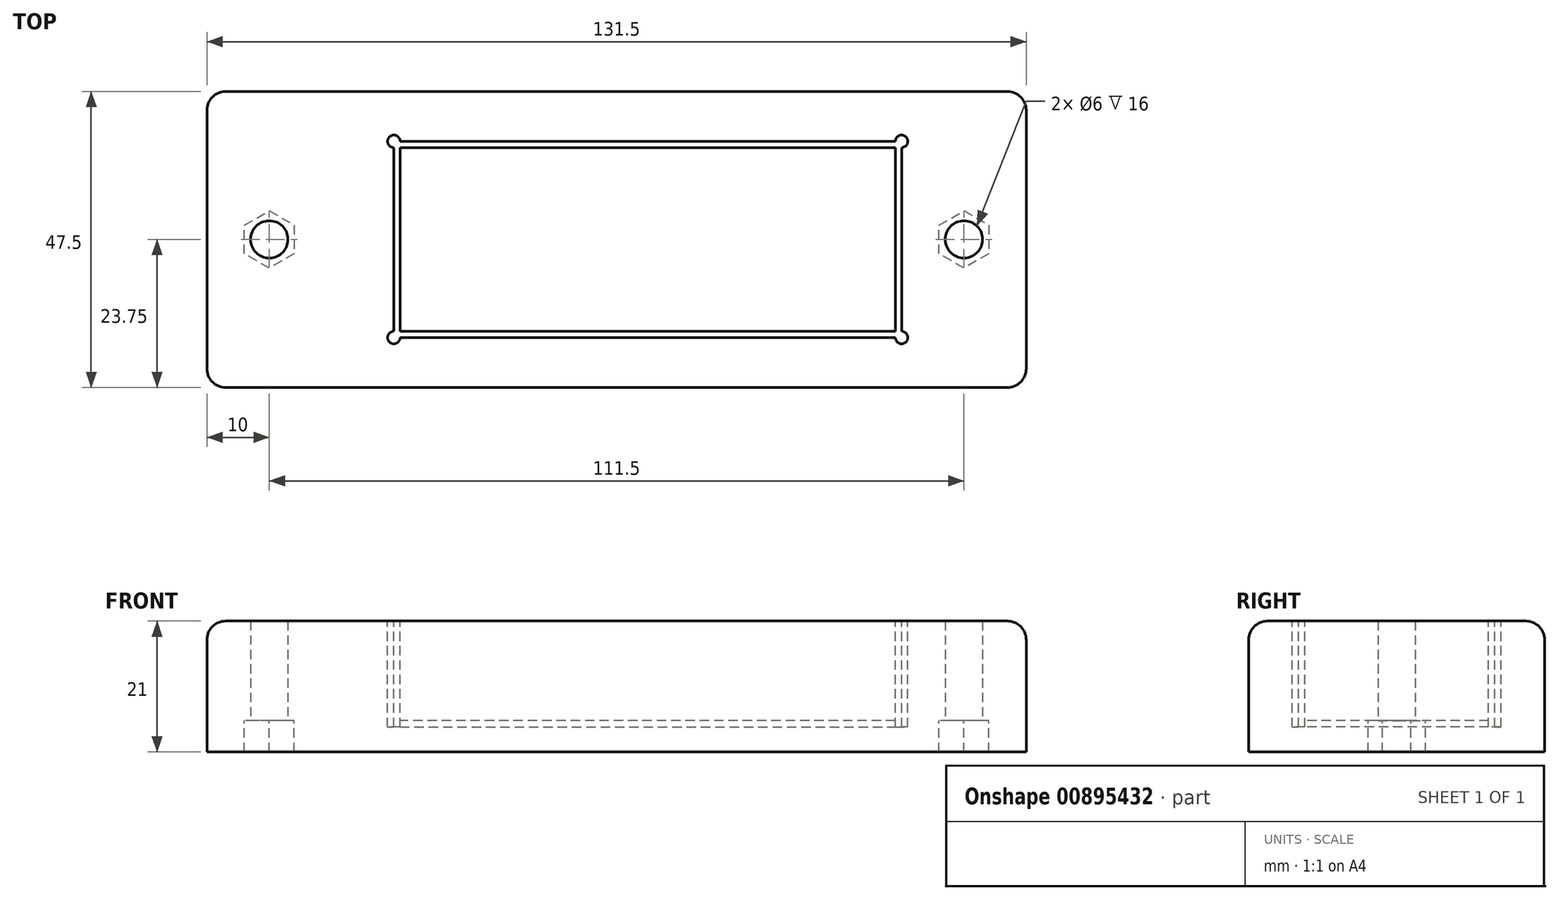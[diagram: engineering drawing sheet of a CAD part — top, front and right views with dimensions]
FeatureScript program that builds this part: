
annotation { "Feature Type Name" : "Feature", "Feature Type Description" : "" }
export const myFeature = defineFeature(function(context is Context, id is Id, definition is map)
    precondition{}
    {
        {
            var Q0;
            Q0=qCreatedBy(makeId("Top.planeOp"),FACE);
            var sketch = newSketch(context, id + "F0", { "sketchPlane" : qUnion([Q0])});
            skLineSegment(sketch, "E0.bottom", {"start": v(-35.75, 15.75) * mm, "end": v(40.25, 15.75) * mm});
            skLineSegment(sketch, "E0.top", {"start": v(-35.75, -15.75) * mm, "end": v(20.25, -15.75) * mm});
            skLineSegment(sketch, "E0.left", {"start": v(-35.75, 15.75) * mm, "end": v(-35.75, -15.75) * mm});
            skLineSegment(sketch, "E1.bottom", {"start": v(-65.75, 23.75) * mm, "end": v(65.75, 23.75) * mm});
            skLineSegment(sketch, "E1.top", {"start": v(-65.75, -23.75) * mm, "end": v(65.75, -23.75) * mm});
            skLineSegment(sketch, "E1.left", {"start": v(-65.75, 23.75) * mm, "end": v(-65.75, -23.75) * mm});
            skLineSegment(sketch, "E1.right", {"start": v(65.75, 23.75) * mm, "end": v(65.75, -23.75) * mm});
            skLineSegment(sketch, "E2", {"start": v(40.25, 15.75) * mm, "end": v(65.75, 15.75) * mm});
            skLineSegment(sketch, "E3", {"start": v(20.25, -15.75) * mm, "end": v(65.75, -15.75) * mm});
            skLineSegment(sketch, "E4", {"start": v(45.75, 15.75) * mm, "end": v(45.75, -15.75) * mm});
            skCircle(sketch, "E5.cCircle", {"center": v(-55.75, 0) * mm, "radius": 3.98 * mm, "construction": true});
            skLineSegment(sketch, "E5.0", {"start": v(-55.75, -4.6) * mm, "end": v(-59.73, -2.3) * mm});
            skLineSegment(sketch, "E5.1", {"start": v(-59.73, -2.3) * mm, "end": v(-59.73, 2.3) * mm});
            skLineSegment(sketch, "E5.2", {"start": v(-59.73, 2.3) * mm, "end": v(-55.75, 4.6) * mm});
            skLineSegment(sketch, "E5.3", {"start": v(-55.75, 4.6) * mm, "end": v(-51.77, 2.3) * mm});
            skLineSegment(sketch, "E5.4", {"start": v(-51.77, 2.3) * mm, "end": v(-51.77, -2.3) * mm});
            skLineSegment(sketch, "E5.5", {"start": v(-51.77, -2.3) * mm, "end": v(-55.75, -4.6) * mm});
            skPoint(sketch, "E5.0.midPoint", {"position": v(-57.74, -3.45) * mm});
            skLineSegment(sketch, "E6", {"start": v(-65.75, -23.75) * mm, "end": v(65.75, 23.75) * mm, "construction": true});
            skLineSegment(sketch, "E7", {"start": v(65.75, -23.75) * mm, "end": v(-65.75, 23.75) * mm, "construction": true});
            skPoint(sketch, "E8", {"position": v(0, 0) * mm});
            skCircle(sketch, "E9.cCircle", {"center": v(55.75, 0) * mm, "radius": 3.98 * mm, "construction": true});
            skLineSegment(sketch, "E9.0", {"start": v(55.75, -4.6) * mm, "end": v(51.77, -2.3) * mm});
            skLineSegment(sketch, "E9.1", {"start": v(51.77, -2.3) * mm, "end": v(51.77, 2.3) * mm});
            skLineSegment(sketch, "E9.2", {"start": v(51.77, 2.3) * mm, "end": v(55.75, 4.6) * mm});
            skLineSegment(sketch, "E9.3", {"start": v(55.75, 4.6) * mm, "end": v(59.73, 2.3) * mm});
            skLineSegment(sketch, "E9.4", {"start": v(59.73, 2.3) * mm, "end": v(59.73, -2.3) * mm});
            skLineSegment(sketch, "E9.5", {"start": v(59.73, -2.3) * mm, "end": v(55.75, -4.6) * mm});
            skPoint(sketch, "E9.0.midPoint", {"position": v(53.76, -3.45) * mm});
            skCircle(sketch, "E10", {"center": v(55.75, 0) * mm, "radius": 3 * mm});
            skCircle(sketch, "E11", {"center": v(-55.75, 0) * mm, "radius": 3 * mm});
            skSolve(sketch);
        }
        {
            var Q0;
            {var subQ2=sQuery(id+"F0.wireOp",EDGE,"E0.bottom");Q0=makeQuery(id+"F0.imprint","IMPRINT",FACE,{"disambiguationData":[TD([[makeQuery(id+"F0.imprint","IMPRINT",EDGE,{"derivedFrom":subQ2}),1.0]])]});}
            var Q1;
            {var subQ0=sQuery(id+"F0.wireOp",EDGE,"E4");Q1=makeQuery(id+"F0.imprint","IMPRINT",FACE,{"disambiguationData":[TD([[makeQuery(id+"F0.imprint","IMPRINT",EDGE,{"derivedFrom":subQ0}),1.0]])]});}
            var Q2;
            Q2=makeQuery(id+"F0.imprint","IMPRINT",FACE,{"disambiguationData":[TD([[makeQuery(id+"F0.imprint","IMPRINT",EDGE,{"derivedFrom":sQuery(id+"F0.wireOp",EDGE,"E5.0")}),-1.0]])]});
            var Q3;
            Q3=makeQuery(id+"F0.imprint","IMPRINT",FACE,{"disambiguationData":[TD([[makeQuery(id+"F0.imprint","IMPRINT",EDGE,{"derivedFrom":sQuery(id+"F0.wireOp",EDGE,"E9.0")}),-1.0]])]});
            extrude(context, id + "F1", {"entities" : qUnion([Q0, Q1, Q2, Q3]), "depth" : 16 * mm, "offsetDistance" : 25 * mm});
        }
        {
            var Q0;
            Q0 = qSketchRegion(id + "F0", true);
            var Q1;
            Q1=makeQuery(id+"F0.imprint","IMPRINT",FACE,{"disambiguationData":[TD([[makeQuery(id+"F0.imprint","IMPRINT",EDGE,{"derivedFrom":sQuery(id+"F0.wireOp",EDGE,"E0.bottom")}),-1.0]])]});
            var Q2;
            {var subQ0=sQuery(id+"F0.wireOp",EDGE,"E0.right");Q2=makeQuery(id+"F0.imprint","IMPRINT",FACE,{"disambiguationData":[TD([[makeQuery(id+"F0.imprint","IMPRINT",EDGE,{"derivedFrom":subQ0}),1.0]])]});}
            extrude(context, id + "F2", {"entities" : qUnion([Q0, Q1, Q2]), "operationType" : NewBodyOperationType.ADD, "oppositeDirection" : true, "depth" : 5 * mm, "offsetDistance" : 25 * mm});
        }
        {
            var Q0;
            Q0=makeQuery(id+"F0.imprint","IMPRINT",FACE,{"disambiguationData":[TD([[makeQuery(id+"F0.imprint","IMPRINT",EDGE,{"derivedFrom":sQuery(id+"F0.wireOp",EDGE,"E0.bottom")}),-1.0]])]});
            var sketch = newSketch(context, id + "F3", { "sketchPlane" : qUnion([Q0])});
            skLineSegment(sketch, "E12.bottom", {"start": v(44.75, 14.75) * mm, "end": v(-34.75, 14.75) * mm});
            skLineSegment(sketch, "E12.top", {"start": v(44.75, -14.75) * mm, "end": v(-34.75, -14.75) * mm});
            skLineSegment(sketch, "E12.left", {"start": v(44.75, 14.75) * mm, "end": v(44.75, -14.75) * mm});
            skLineSegment(sketch, "E12.right", {"start": v(-34.75, 14.75) * mm, "end": v(-34.75, -14.75) * mm});
            skPoint(sketch, "E12.middle", {"position": v(0, 0) * mm});
            skSolve(sketch);
        }
        {
            var Q0;
            Q0=makeQuery(id+"F3.imprint","IMPRINT",FACE,{"disambiguationData":[TD([[makeQuery(id+"F3.imprint","IMPRINT",EDGE,{"derivedFrom":sQuery(id+"F3.wireOp",EDGE,"E12.bottom")}),-1.0]])]});
            extrude(context, id + "F4", {"entities" : qUnion([Q0]), "operationType" : NewBodyOperationType.REMOVE, "oppositeDirection" : true, "depth" : 1 * mm, "offsetDistance" : 25 * mm});
        }
        {
            var Q0;
            Q0=makeQuery(id+"F1.opExtrude","CAP_FACE",FACE,{"disambiguationData":[OSD([sQuery(id+"F0.wireOp",EDGE,"E0.bottom"),sQuery(id+"F0.wireOp",EDGE,"E0.top"),sQuery(id+"F0.wireOp",EDGE,"E0.left"),sQuery(id+"F0.wireOp",EDGE,"E1.bottom"),sQuery(id+"F0.wireOp",EDGE,"E1.top"),sQuery(id+"F0.wireOp",EDGE,"E1.left"),sQuery(id+"F0.wireOp",EDGE,"E1.right"),sQuery(id+"F0.wireOp",EDGE,"E3"),sQuery(id+"F0.wireOp",EDGE,"E4"),sQuery(id+"F0.wireOp",EDGE,"E10"),sQuery(id+"F0.wireOp",EDGE,"E11")])],"isStart":false});
            var sketch = newSketch(context, id + "F5", { "sketchPlane" : qUnion([Q0])});
            skCircle(sketch, "E13", {"center": v(45.75, 15.75) * mm, "radius": 1 * mm});
            skCircle(sketch, "E14", {"center": v(45.75, -15.75) * mm, "radius": 1 * mm});
            skCircle(sketch, "E15", {"center": v(-35.75, -15.75) * mm, "radius": 1 * mm});
            skCircle(sketch, "E16", {"center": v(-35.75, 15.75) * mm, "radius": 1 * mm});
            skSolve(sketch);
        }
        {
            var Q0;
            Q0 = qSketchRegion(id + "F5", true);
            var Q1;
            Q1=makeQuery(id+"F4.boolean.opBoolean","COPY",FACE,{"derivedFrom":makeQuery(id+"F4.opExtrude","CAP_FACE",FACE,{"disambiguationData":[OSD([sQuery(id+"F0.wireOp",EDGE,"E0.bottom"),sQuery(id+"F0.wireOp",EDGE,"E0.top"),sQuery(id+"F0.wireOp",EDGE,"E0.left"),sQuery(id+"F0.wireOp",EDGE,"E3"),sQuery(id+"F0.wireOp",EDGE,"E4"),sQuery(id+"F3.wireOp",EDGE,"E12.bottom"),sQuery(id+"F3.wireOp",EDGE,"E12.top"),sQuery(id+"F3.wireOp",EDGE,"E12.left"),sQuery(id+"F3.wireOp",EDGE,"E12.right")])],"isStart":false})});
            extrude(context, id + "F6", {"entities" : qUnion([Q0]), "operationType" : NewBodyOperationType.REMOVE, "endBound" : BoundingType.UP_TO_SURFACE, "oppositeDirection" : true, "depth" : 25 * mm, "endBoundEntityFace" : qUnion([Q1]), "offsetDistance" : 25 * mm});
        }
        {
            var Q0;
            {var subQ0=sQuery(id+"F0.wireOp",EDGE,"E1.right");var subQ1=sQuery(id+"F0.wireOp",EDGE,"E1.bottom");Q0=makeQuery(id+"F2.boolean.opBoolean","MERGE",EDGE,{"derivedFrom":[makeQuery(id+"F1.opExtrude","SWEPT_EDGE",EDGE,{"disambiguationData":[OSD([subQ1,subQ0])]}),makeQuery(id+"F2.opExtrude","SWEPT_EDGE",EDGE,{"disambiguationData":[OSD([subQ1,subQ0])]})]});}
            var Q1;
            Q1=makeQuery(id+"F1.opExtrude","CAP_EDGE",EDGE,{"disambiguationData":[OSD([sQuery(id+"F0.wireOp",EDGE,"E1.right")])],"isStart":false});
            var Q2;
            Q2=makeQuery(id+"F1.opExtrude","CAP_EDGE",EDGE,{"disambiguationData":[OSD([sQuery(id+"F0.wireOp",EDGE,"E1.bottom")])],"isStart":false});
            var Q3;
            Q3=makeQuery(id+"F1.opExtrude","CAP_EDGE",EDGE,{"disambiguationData":[OSD([sQuery(id+"F0.wireOp",EDGE,"E1.top")])],"isStart":false});
            var Q4;
            {var subQ0=sQuery(id+"F0.wireOp",EDGE,"E1.right");var subQ1=sQuery(id+"F0.wireOp",EDGE,"E1.top");Q4=makeQuery(id+"F2.boolean.opBoolean","MERGE",EDGE,{"derivedFrom":[makeQuery(id+"F1.opExtrude","SWEPT_EDGE",EDGE,{"disambiguationData":[OSD([subQ1,subQ0])]}),makeQuery(id+"F2.opExtrude","SWEPT_EDGE",EDGE,{"disambiguationData":[OSD([subQ1,subQ0])]})]});}
            var Q5;
            {var subQ0=sQuery(id+"F0.wireOp",EDGE,"E1.left");var subQ1=sQuery(id+"F0.wireOp",EDGE,"E1.top");Q5=makeQuery(id+"F2.boolean.opBoolean","MERGE",EDGE,{"derivedFrom":[makeQuery(id+"F1.opExtrude","SWEPT_EDGE",EDGE,{"disambiguationData":[OSD([subQ1,subQ0])]}),makeQuery(id+"F2.opExtrude","SWEPT_EDGE",EDGE,{"disambiguationData":[OSD([subQ1,subQ0])]})]});}
            var Q6;
            {var subQ0=sQuery(id+"F0.wireOp",EDGE,"E1.left");var subQ1=sQuery(id+"F0.wireOp",EDGE,"E1.bottom");Q6=makeQuery(id+"F2.boolean.opBoolean","MERGE",EDGE,{"derivedFrom":[makeQuery(id+"F1.opExtrude","SWEPT_EDGE",EDGE,{"disambiguationData":[OSD([subQ1,subQ0])]}),makeQuery(id+"F2.opExtrude","SWEPT_EDGE",EDGE,{"disambiguationData":[OSD([subQ1,subQ0])]})]});}
            var Q7;
            Q7=makeQuery(id+"F1.opExtrude","CAP_EDGE",EDGE,{"disambiguationData":[OSD([sQuery(id+"F0.wireOp",EDGE,"E1.left")])],"isStart":false});
            fillet(context, id + "F7", {"entities" : qUnion([Q0, Q1, Q2, Q3, Q4, Q5, Q6, Q7]), "radius" : 3 * mm, "tangentPropagation" : true, "allowEdgeOverflow" : false});
        }
    });
